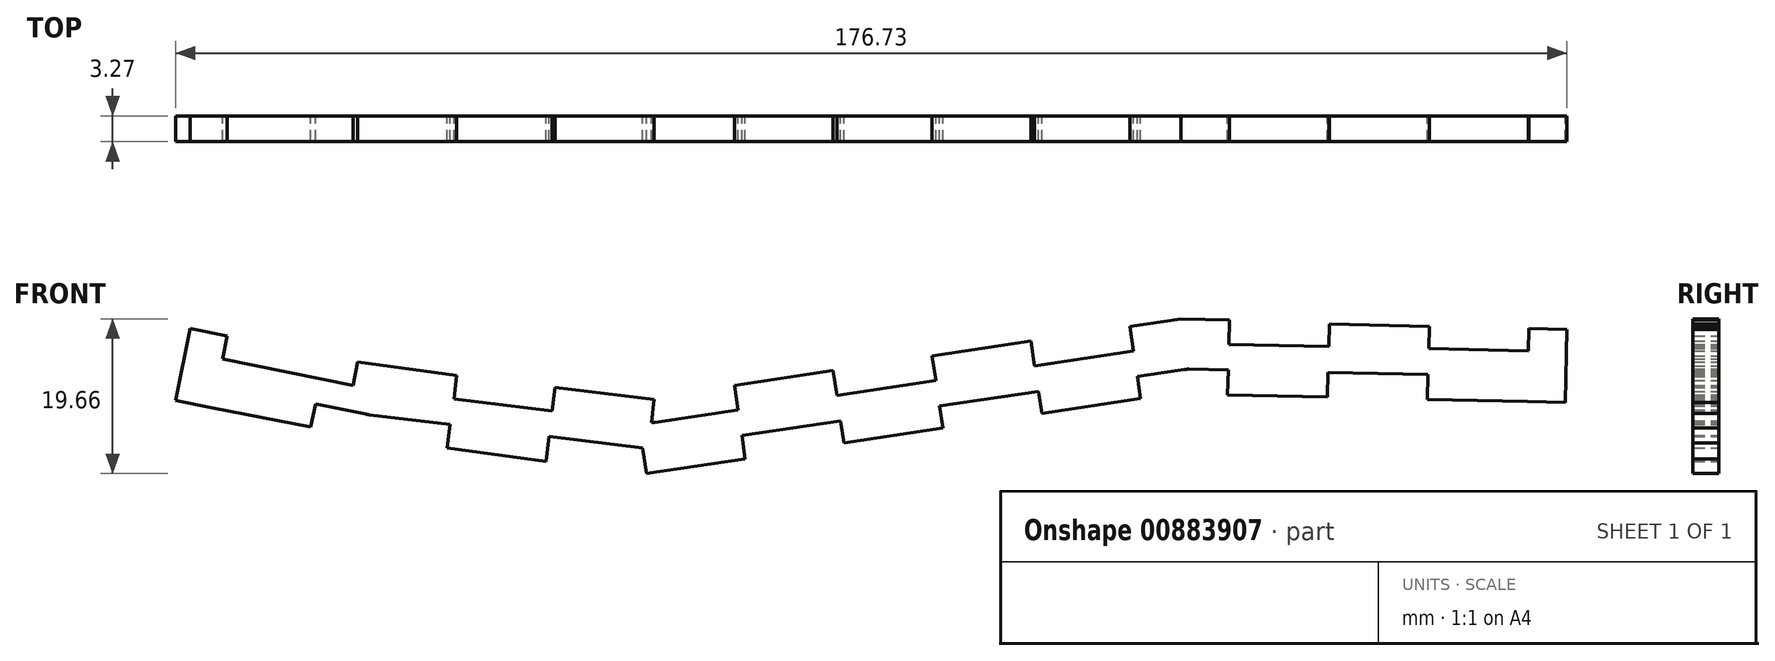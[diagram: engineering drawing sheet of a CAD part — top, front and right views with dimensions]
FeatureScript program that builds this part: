
annotation { "Feature Type Name" : "Feature", "Feature Type Description" : "" }
export const myFeature = defineFeature(function(context is Context, id is Id, definition is map)
    precondition{}
    {
        {
            var Q0;
            Q0=qCreatedBy(makeId("Front.planeOp"),FACE);
            var sketch = newSketch(context, id + "F0", { "sketchPlane" : qUnion([Q0])});
            skPoint(sketch, "E0", {"position": v(-86.3, -2.92) * mm});
            skPoint(sketch, "E1", {"position": v(-86.3, -6.28) * mm});
            skPoint(sketch, "E2", {"position": v(88.08, -2.92) * mm});
            skPoint(sketch, "E3", {"position": v(40.52, -1.9) * mm});
            skPoint(sketch, "E4", {"position": v(-27.27, -12) * mm});
            skPoint(sketch, "E5", {"position": v(-62.83, -7.7) * mm});
            skLineSegment(sketch, "E6", {"start": v(88.08, -2.92) * mm, "end": v(41.08, -1.9) * mm});
            skLineSegment(sketch, "E7", {"start": v(39.98, -1.97) * mm, "end": v(-26.83, -11.93) * mm});
            skLineSegment(sketch, "E8", {"start": v(-27.7, -11.94) * mm, "end": v(-62.7, -7.72) * mm});
            skLineSegment(sketch, "E9", {"start": v(-62.95, -7.68) * mm, "end": v(-81.74, -3.85) * mm});
            skPoint(sketch, "E10", {"position": v(88.08, -6.2) * mm});
            skPoint(sketch, "E11", {"position": v(40.73, -5.17) * mm});
            skPoint(sketch, "E12", {"position": v(-27.22, -15.3) * mm});
            skPoint(sketch, "E13", {"position": v(-63.35, -10.93) * mm});
            skLineSegment(sketch, "E14", {"start": v(88.08, -6.2) * mm, "end": v(41, -5.17) * mm});
            skLineSegment(sketch, "E15", {"start": v(40.46, -5.2) * mm, "end": v(-26.35, -15.16) * mm});
            skLineSegment(sketch, "E16", {"start": v(-28.1, -15.19) * mm, "end": v(-63.09, -10.97) * mm});
            skLineSegment(sketch, "E17", {"start": v(-63.6, -10.88) * mm, "end": v(-82.4, -7.07) * mm});
            skArc(sketch, "E18.filletArc", {"start": v(-62.95, -7.68) * mm, "mid": v(-62.82, -7.7) * mm, "end": v(-62.7, -7.72) * mm});
            skArc(sketch, "E19.filletArc", {"start": v(-63.6, -10.88) * mm, "mid": v(-63.34, -10.93) * mm, "end": v(-63.09, -10.97) * mm});
            skArc(sketch, "E20.filletArc", {"start": v(-27.7, -11.94) * mm, "mid": v(-27.27, -11.96) * mm, "end": v(-26.83, -11.93) * mm});
            skArc(sketch, "E21.filletArc", {"start": v(-28.1, -15.19) * mm, "mid": v(-27.22, -15.23) * mm, "end": v(-26.35, -15.16) * mm});
            skArc(sketch, "E22.filletArc", {"start": v(41, -5.17) * mm, "mid": v(40.73, -5.18) * mm, "end": v(40.46, -5.2) * mm});
            skArc(sketch, "E23.filletArc", {"start": v(41.08, -1.9) * mm, "mid": v(40.53, -1.92) * mm, "end": v(39.98, -1.97) * mm});
            skLineSegment(sketch, "E24", {"start": v(88.08, -2.92) * mm, "end": v(88.08, -6.2) * mm});
            skLineSegment(sketch, "E25", {"start": v(-86.3, -2.92) * mm, "end": v(-86.3, -6.28) * mm});
            skLineSegment(sketch, "E26", {"start": v(-85.85, 0) * mm, "end": v(-81.15, -0.96) * mm});
            skLineSegment(sketch, "E27", {"start": v(-81.15, -0.96) * mm, "end": v(-81.74, -3.85) * mm});
            skLineSegment(sketch, "E28", {"start": v(-83, -10.1) * mm, "end": v(-87.71, -9.15) * mm});
            skLineSegment(sketch, "E29", {"start": v(-87.71, -9.15) * mm, "end": v(-85.85, 0) * mm});
            skLineSegment(sketch, "E30", {"start": v(-82.4, -7.07) * mm, "end": v(-83, -10.1) * mm});
            skLineSegment(sketch, "E31", {"start": v(-81.74, -3.85) * mm, "end": v(-82.4, -7.07) * mm});
            skLineSegment(sketch, "E32", {"start": v(-82.4, -7.07) * mm, "end": v(-86.3, -6.28) * mm});
            skLineSegment(sketch, "E33", {"start": v(-81.74, -3.85) * mm, "end": v(-86.3, -2.92) * mm});
            skPoint(sketch, "E34", {"position": v(-66.43, -13.37) * mm});
            skPoint(sketch, "E35", {"position": v(-64.58, -4.28) * mm});
            skPoint(sketch, "E36", {"position": v(-52, -5.99) * mm});
            skLineSegment(sketch, "E37", {"start": v(-52, -5.99) * mm, "end": v(-52.35, -8.97) * mm});
            skLineSegment(sketch, "E38", {"start": v(-52, -5.99) * mm, "end": v(-64.58, -4.28) * mm});
            skLineSegment(sketch, "E39", {"start": v(-64.58, -4.28) * mm, "end": v(-65.18, -7.22) * mm});
            skLineSegment(sketch, "E40", {"start": v(-52, -5.99) * mm, "end": v(-52.83, -12.2) * mm});
            skLineSegment(sketch, "E41", {"start": v(-53.24, -15.17) * mm, "end": v(-40.65, -16.88) * mm});
            skLineSegment(sketch, "E42", {"start": v(-40.65, -16.88) * mm, "end": v(-40.27, -13.72) * mm});
            skLineSegment(sketch, "E43", {"start": v(-52.83, -12.2) * mm, "end": v(-53.24, -15.17) * mm});
            skLineSegment(sketch, "E44", {"start": v(-40.27, -13.72) * mm, "end": v(-39.52, -7.5) * mm});
            skLineSegment(sketch, "E45", {"start": v(-39.52, -7.5) * mm, "end": v(-26.9, -9.01) * mm});
            skLineSegment(sketch, "E46", {"start": v(-26.9, -9.01) * mm, "end": v(-27.33, -12.53) * mm});
            skLineSegment(sketch, "E47", {"start": v(-27.33, -12.53) * mm, "end": v(-27.66, -15.22) * mm});
            skLineSegment(sketch, "E48", {"start": v(-27.91, -18.43) * mm, "end": v(-15.35, -16.56) * mm});
            skLineSegment(sketch, "E49", {"start": v(-15.35, -16.56) * mm, "end": v(-15.8, -13.59) * mm});
            skLineSegment(sketch, "E50", {"start": v(-15.8, -13.59) * mm, "end": v(-16.74, -7.22) * mm});
            skLineSegment(sketch, "E51", {"start": v(-16.74, -7.22) * mm, "end": v(-4.18, -5.35) * mm});
            skLineSegment(sketch, "E52", {"start": v(-4.18, -5.35) * mm, "end": v(-2.81, -14.52) * mm});
            skLineSegment(sketch, "E53", {"start": v(-2.81, -14.52) * mm, "end": v(9.75, -12.65) * mm});
            skLineSegment(sketch, "E54", {"start": v(9.75, -12.65) * mm, "end": v(8.38, -3.48) * mm});
            skLineSegment(sketch, "E55", {"start": v(8.38, -3.48) * mm, "end": v(20.94, -1.6) * mm});
            skLineSegment(sketch, "E56", {"start": v(20.94, -1.6) * mm, "end": v(22.3, -10.78) * mm});
            skLineSegment(sketch, "E57", {"start": v(22.3, -10.78) * mm, "end": v(34.87, -8.9) * mm});
            skLineSegment(sketch, "E58", {"start": v(34.87, -8.9) * mm, "end": v(33.5, 0.26) * mm});
            skLineSegment(sketch, "E59", {"start": v(33.5, 0.26) * mm, "end": v(39.98, 1.23) * mm});
            skLineSegment(sketch, "E60", {"start": v(39.98, 1.23) * mm, "end": v(46.13, 1.1) * mm});
            skLineSegment(sketch, "E61", {"start": v(46.13, 1.1) * mm, "end": v(45.93, -8.44) * mm});
            skLineSegment(sketch, "E62", {"start": v(45.93, -8.44) * mm, "end": v(58.62, -8.72) * mm});
            skLineSegment(sketch, "E63", {"start": v(58.62, -8.72) * mm, "end": v(58.82, 0.55) * mm});
            skLineSegment(sketch, "E64", {"start": v(58.82, 0.55) * mm, "end": v(71.52, 0.27) * mm});
            skLineSegment(sketch, "E65", {"start": v(71.52, 0.27) * mm, "end": v(71.32, -9) * mm});
            skLineSegment(sketch, "E66", {"start": v(71.32, -9) * mm, "end": v(84.02, -9.27) * mm});
            skLineSegment(sketch, "E67", {"start": v(84.02, -9.27) * mm, "end": v(84.22, 0) * mm});
            skLineSegment(sketch, "E68", {"start": v(84.22, 0) * mm, "end": v(89.02, -0.1) * mm});
            skLineSegment(sketch, "E69", {"start": v(89.02, -0.1) * mm, "end": v(88.82, -9.37) * mm});
            skLineSegment(sketch, "E70", {"start": v(88.82, -9.37) * mm, "end": v(84.02, -9.27) * mm});
            skLineSegment(sketch, "E71", {"start": v(-27.91, -18.43) * mm, "end": v(-28.4, -15.15) * mm});
            skLineSegment(sketch, "E72", {"start": v(-65.18, -7.22) * mm, "end": v(-66.43, -13.37) * mm});
            skLineSegment(sketch, "E73", {"start": v(-82.4, -7.07) * mm, "end": v(-69.94, -9.6) * mm});
            skLineSegment(sketch, "E74", {"start": v(-69.94, -9.6) * mm, "end": v(-70.54, -12.53) * mm});
            skLineSegment(sketch, "E75", {"start": v(-70.54, -12.53) * mm, "end": v(-83, -10.1) * mm});
            skSolve(sketch);
        }
        {
            var Q0;
            Q0 = qSketchRegion(id + "F0", true);
            extrude(context, id + "F1", {"entities" : qUnion([Q0]), "depth" : 3.27 * mm, "offsetDistance" : 25 * mm});
        }
    });
